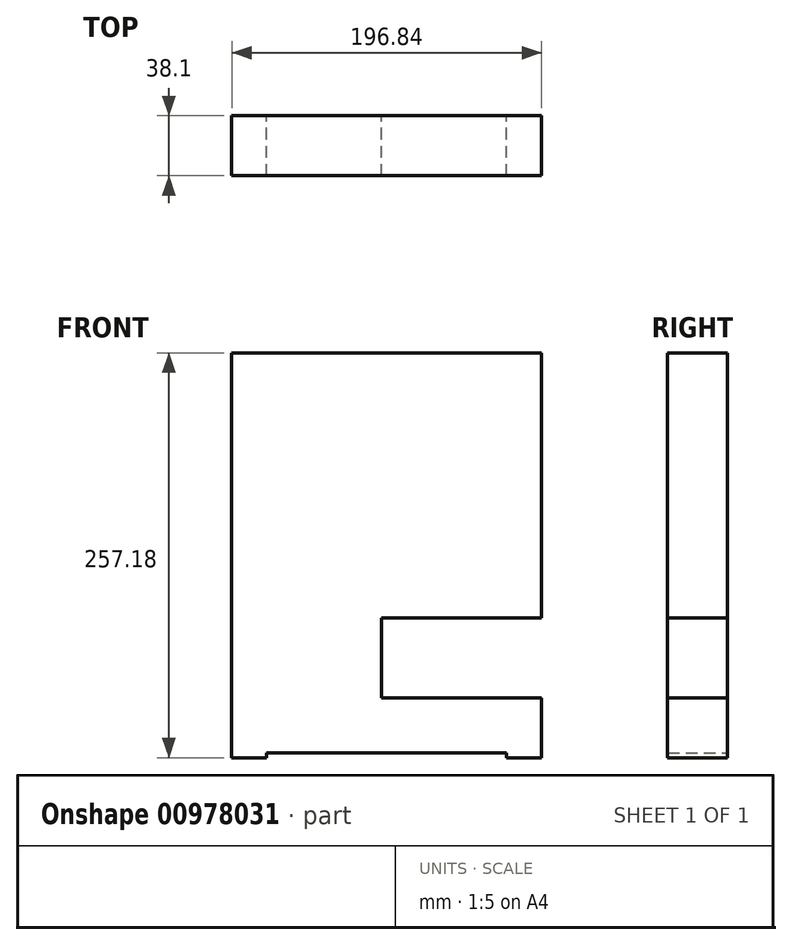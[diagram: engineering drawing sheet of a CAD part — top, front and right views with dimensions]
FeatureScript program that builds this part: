
annotation { "Feature Type Name" : "Feature", "Feature Type Description" : "" }
export const myFeature = defineFeature(function(context is Context, id is Id, definition is map)
    precondition{}
    {
        {
            var Q0;
            Q0=qCreatedBy(makeId("Front.planeOp"),FACE);
            var sketch = newSketch(context, id + "F0", { "sketchPlane" : qUnion([Q0])});
            skLineSegment(sketch, "E0", {"start": v(0, 128.59) * mm, "end": v(0, -128.59) * mm, "construction": true});
            skLineSegment(sketch, "E1", {"start": v(-98.42, 0) * mm, "end": v(98.43, 0) * mm, "construction": true});
            skLineSegment(sketch, "E2.bottom", {"start": v(-98.42, 128.59) * mm, "end": v(98.43, 128.59) * mm});
            skLineSegment(sketch, "E2.top", {"start": v(-98.42, -128.59) * mm, "end": v(98.43, -128.59) * mm});
            skLineSegment(sketch, "E2.left", {"start": v(-98.42, 128.59) * mm, "end": v(-98.42, -128.59) * mm});
            skLineSegment(sketch, "E2.right", {"start": v(98.43, 128.59) * mm, "end": v(98.43, -128.59) * mm});
            skLineSegment(sketch, "E3.bottom", {"start": v(-76.2, -128.59) * mm, "end": v(76.2, -128.59) * mm});
            skLineSegment(sketch, "E3.top", {"start": v(-76.2, -125.41) * mm, "end": v(76.2, -125.41) * mm});
            skLineSegment(sketch, "E3.left", {"start": v(-76.2, -128.59) * mm, "end": v(-76.2, -125.41) * mm});
            skLineSegment(sketch, "E3.right", {"start": v(76.2, -128.59) * mm, "end": v(76.2, -125.41) * mm});
            skLineSegment(sketch, "E4.bottom", {"start": v(98.43, -39.69) * mm, "end": v(-3.17, -39.69) * mm});
            skLineSegment(sketch, "E4.top", {"start": v(98.43, -90.49) * mm, "end": v(-3.17, -90.49) * mm});
            skLineSegment(sketch, "E4.left", {"start": v(98.43, -39.69) * mm, "end": v(98.43, -90.49) * mm});
            skLineSegment(sketch, "E4.right", {"start": v(-3.17, -39.69) * mm, "end": v(-3.17, -90.49) * mm});
            skSolve(sketch);
        }
        {
            var Q0;
            {var subQ8=sQuery(id+"F0.wireOp",EDGE,"E2.bottom");Q0=makeQuery(id+"F0.imprint","IMPRINT",FACE,{"disambiguationData":[TD([[makeQuery(id+"F0.imprint","IMPRINT",EDGE,{"derivedFrom":subQ8}),-1.0]])]});}
            extrude(context, id + "F1", {"entities" : qUnion([Q0]), "depth" : 38.1 * mm, "offsetDistance" : 25.4 * mm});
        }
    });
